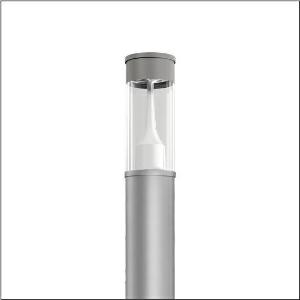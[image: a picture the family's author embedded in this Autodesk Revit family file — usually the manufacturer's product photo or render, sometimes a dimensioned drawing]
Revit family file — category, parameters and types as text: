
# Revit family: city-light_260_iq___pl1_2s_5xa5295of14h_8957
name_source: partatom
category: Lighting Fixtures
units: mm (PartAtom-declared; Revit-internal decimal feet)

## family parameters
Cut with Voids When Loaded = No
Host = Face
Light Source = No
Part Type = Normal
Room Calculation Point = No
Round Connector Dimension = Use Diameter
Shared = No

## types (1)
- --- (1 x LED, 2970 lm, 21.8 W, 2700K)
    Apparent Load = 22 VA
    CIE Flux Codes = 23 62 94 96 100
    Color Rendering = 70
    Color Temperature = 2700K
    Default Elevation = 1800 mm
    Description = City-Light 260 iQ, light pillar, Module 540 iQ-SR, primary light control with 3 zone facetted reflector, of plastic, silver coated, highly specular, structured, primary optical cover: cover, of PMMA, transparent, partly coated, light distribution: PL1.2s, primary light characteristic: symmetric, LED, High Power LED, rated luminous flux: 2.970lm, luminous efficacy: 136lm/W, light colour: 727, colour temperature: 2700K, control gear: ECG iQ, control: pre-setting: logarithmic dimming characteristic, Street-Remote, Auto-Match, Temp-Guard, Lumen-Switch, Night-Set, Smart-Wire, Light-Fading, Desk-Remote (wireless, voltage-free reading and setting of iQ features in the workshop via application-optimized NFC function/RFID function), optimised constant luminous flux control (CLO 2.0), with terminal, 6-pole, max. 2.5mm², mains connection: 230..240V, AC, 50/60Hz, start of lifetime: 22W, end of service life: 23W, reduction: 11W, luminaire housing, cylindrical, of extruded aluminium section, coated, Siteco® metallic grey (DB 702S), length: 2.600mm, diameter: 200mm, Module 540 iQ-SR, traffic white (RAL 9016), equipment: standard, protection rating (complete): IP65, insulation class (complete): insulation class II (safety insulation), certification: CE, ENEC, VDE, packaging unit: 1 piece

Light Distribution: PL1.2s
    Height = 500 mm
    Lamp = 1 x LED
    Lamp Light Flux = 2970 lm
    Lamp Power = 21.8 W
    Lamp count = 1
    Length = 200 mm  [stored 0.656168 ft]
    Luminous efficacy = 136 lm/W
    Manufacturer = Siteco
    ModVariant = No
    Model = 5XA5295OF14H
    Mounting Place = Floor
    Mounting Type = Freestanding
    Number of Poles = 1
    OnlyDefault = Yes
    Power Factor = 1
    Product Name = City-Light 260 iQ | PL1.2s
    Product group = light pillar
    ProductGroupID = 1301
    Protection Class = Protection class II
    Protection Degree = IP 65
    RLX_Detail_Level = 1
    RLX_Emergency_Light_Flux = 0 lm
    RLX_Emergency_Type = 0
    RLX_Emergency_Type_DB = No
    RlxData = <blob elided: 28681 chars, md5=8821cda5>
    Socket = socket
    Standby Power = 0 W
    System Light Flux = 2970 lm
    System Power = 22 W
    Type Comments = factory setting: luminous flux: 100 % | dim-lin: 254 | 456 mA
    Type Image = l_1006920.jpg
    URL = http://relux.com
    VarID = @adj_114867
    Voltage = 0 V
    Weight = 0.00 kg
    Width = 0 mm  [stored 0 ft]

note: [stored X ft] marks values corroborated as IEEE doubles in the binary element streams (Revit-internal decimal feet)

## geometry (parser evidence)
native form markers: Blend x4, Sweep x9
no freeform markers — native parametric forms only
